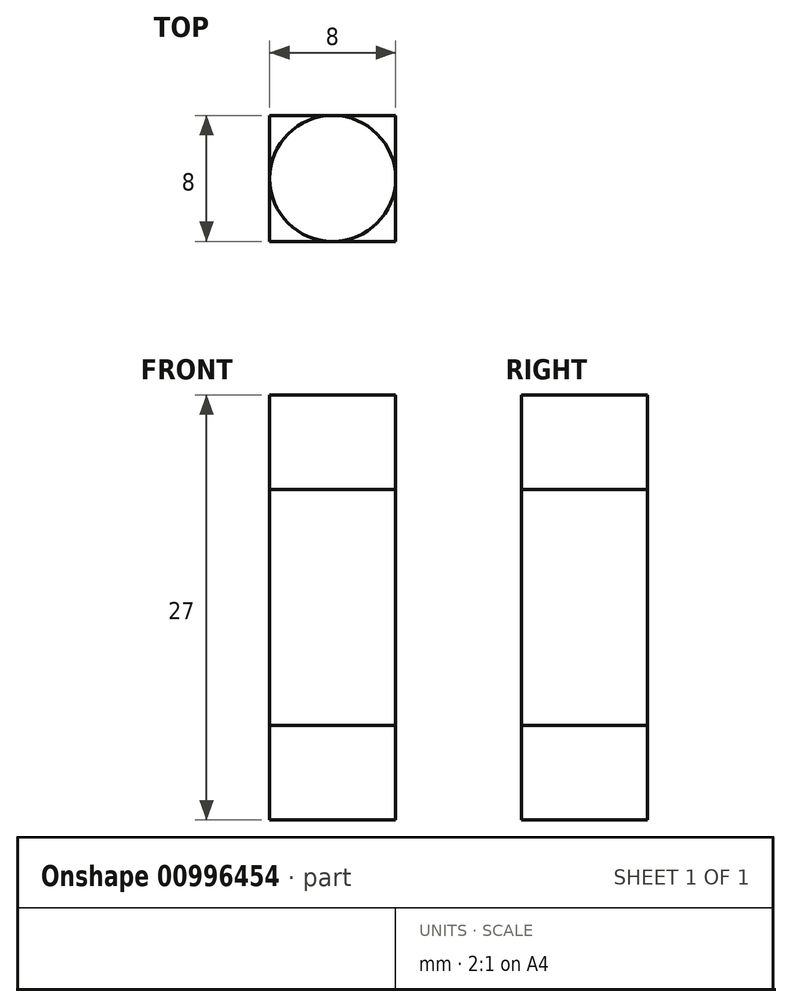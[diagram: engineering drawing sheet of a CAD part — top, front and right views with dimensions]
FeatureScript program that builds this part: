
annotation { "Feature Type Name" : "Feature", "Feature Type Description" : "" }
export const myFeature = defineFeature(function(context is Context, id is Id, definition is map)
    precondition{}
    {
        {
            var Q0;
            Q0=qCreatedBy(makeId("Top.planeOp"),FACE);
            var sketch = newSketch(context, id + "F0", { "sketchPlane" : qUnion([Q0])});
            skCircle(sketch, "E0", {"center": v(0, 0) * mm, "radius": 4 * mm});
            skSolve(sketch);
        }
        {
            var Q0;
            Q0=qSketchRegion(id+"F0",true);
            extrude(context, id + "F1", {"entities" : qUnion([Q0]), "depth" : 6 * mm, "offsetDistance" : 25 * mm});
        }
        {
            var Q0;
            Q0=makeQuery(id+"F1.opExtrude","CAP_FACE",FACE,{"disambiguationData":[OSD([sQuery(id+"F0.wireOp",EDGE,"E0")])],"isStart":false});
            var sketch = newSketch(context, id + "F2", { "sketchPlane" : qUnion([Q0])});
            skLineSegment(sketch, "E1.bottom", {"start": v(4, 4) * mm, "end": v(-4, 4) * mm});
            skLineSegment(sketch, "E1.top", {"start": v(4, -4) * mm, "end": v(-4, -4) * mm});
            skLineSegment(sketch, "E1.left", {"start": v(4, 4) * mm, "end": v(4, -4) * mm});
            skLineSegment(sketch, "E1.right", {"start": v(-4, 4) * mm, "end": v(-4, -4) * mm});
            skPoint(sketch, "E1.middle", {"position": v(0, 0) * mm});
            skSolve(sketch);
        }
        {
            var Q0;
            Q0=qSketchRegion(id+"F2",true);
            extrude(context, id + "F3", {"entities" : qUnion([Q0]), "operationType" : NewBodyOperationType.ADD, "depth" : 15 * mm, "offsetDistance" : 25 * mm});
        }
        {
            var Q0;
            Q0=makeQuery(id+"F3.opExtrude","CAP_FACE",FACE,{"disambiguationData":[OSD([sQuery(id+"F2.wireOp",EDGE,"E1.bottom"),sQuery(id+"F2.wireOp",EDGE,"E1.top"),sQuery(id+"F2.wireOp",EDGE,"E1.left"),sQuery(id+"F2.wireOp",EDGE,"E1.right")])],"isStart":false});
            var sketch = newSketch(context, id + "F4", { "sketchPlane" : qUnion([Q0])});
            skCircle(sketch, "E2", {"center": v(0, 0) * mm, "radius": 4 * mm});
            skSolve(sketch);
        }
        {
            var Q0;
            Q0=qSketchRegion(id+"F4",true);
            extrude(context, id + "F5", {"entities" : qUnion([Q0]), "operationType" : NewBodyOperationType.ADD, "depth" : 6 * mm, "offsetDistance" : 25 * mm});
        }
    });
